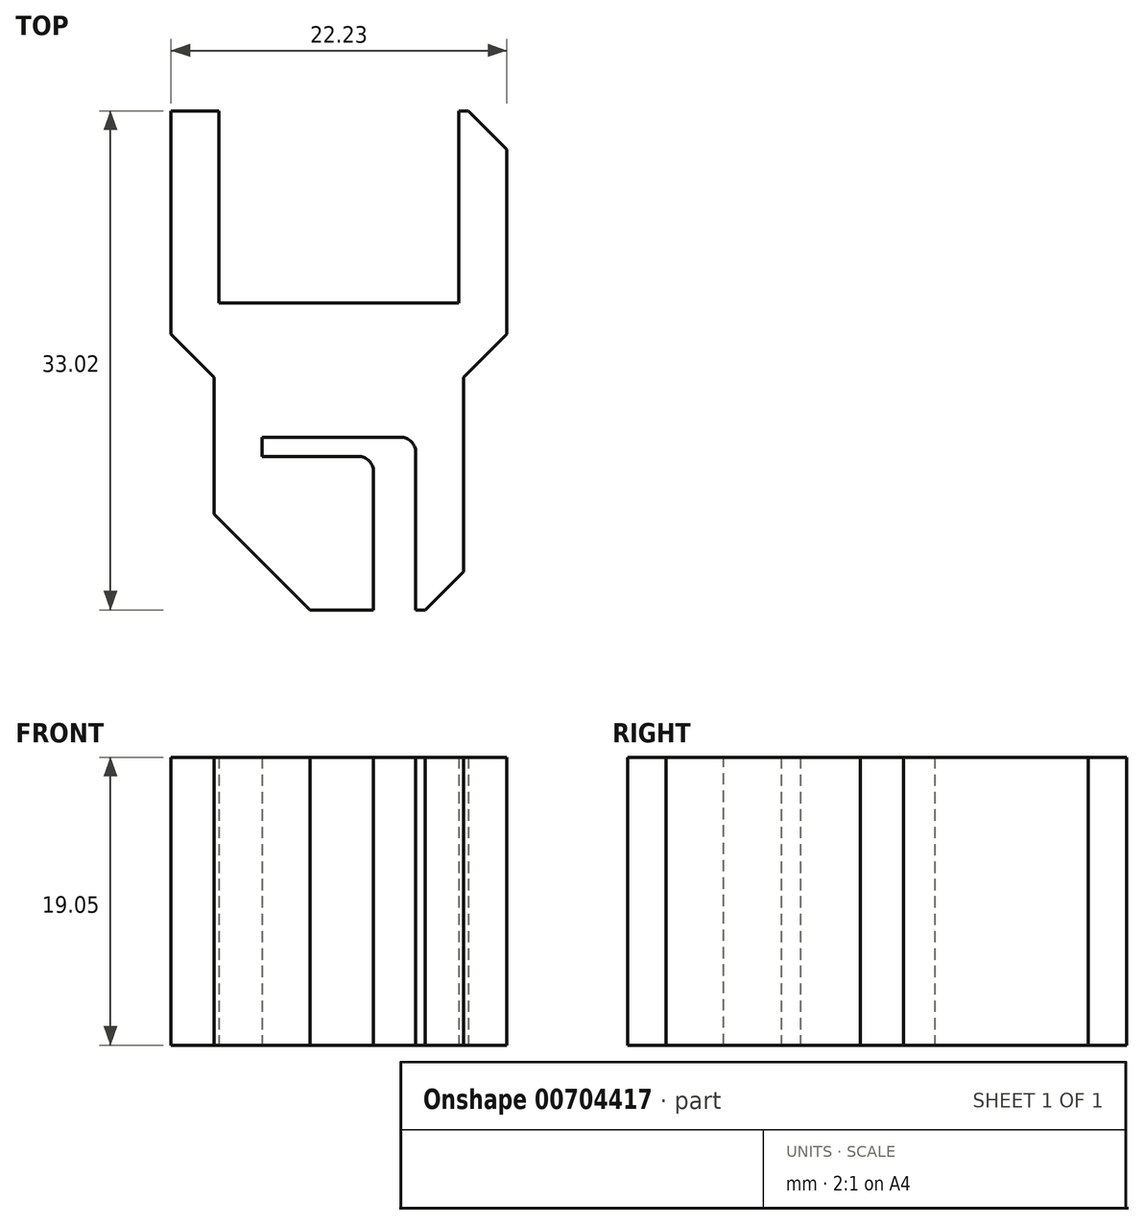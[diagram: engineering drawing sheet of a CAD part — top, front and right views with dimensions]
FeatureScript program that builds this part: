
annotation { "Feature Type Name" : "Feature", "Feature Type Description" : "" }
export const myFeature = defineFeature(function(context is Context, id is Id, definition is map)
    precondition{}
    {
        {
            var Q0;
            Q0=qCreatedBy(makeId("Top.planeOp"),FACE);
            var sketch = newSketch(context, id + "F0", { "sketchPlane" : qUnion([Q0])});
            skLineSegment(sketch, "E0", {"start": v(0, 0) * mm, "end": v(0, 20.47) * mm});
            skLineSegment(sketch, "E1", {"start": v(0, 20.47) * mm, "end": v(-2.86, 20.47) * mm});
            skLineSegment(sketch, "E2", {"start": v(-2.86, 20.47) * mm, "end": v(-2.86, 33.02) * mm});
            skLineSegment(sketch, "E3", {"start": v(-2.86, 33.02) * mm, "end": v(0.32, 33.02) * mm});
            skLineSegment(sketch, "E4", {"start": v(0.32, 33.02) * mm, "end": v(0.32, 20.32) * mm});
            skLineSegment(sketch, "E5", {"start": v(0.32, 20.32) * mm, "end": v(8.26, 20.32) * mm});
            skLineSegment(sketch, "E6", {"start": v(0, 0) * mm, "end": v(3.18, 0) * mm});
            skLineSegment(sketch, "E7", {"start": v(3.18, 0) * mm, "end": v(3.18, 11.43) * mm});
            skLineSegment(sketch, "E8", {"start": v(3.18, 11.43) * mm, "end": v(8.26, 11.43) * mm});
            skLineSegment(sketch, "E9", {"start": v(8.26, 20.32) * mm, "end": v(8.26, 11.43) * mm, "construction": true});
            skLineSegment(sketch, "E10.MirrorCS", {"start": v(13.34, 11.43) * mm, "end": v(8.26, 11.43) * mm});
            skLineSegment(sketch, "E11.MirrorCS", {"start": v(16.51, 20.47) * mm, "end": v(19.37, 20.47) * mm});
            skLineSegment(sketch, "E12.MirrorCS", {"start": v(19.37, 33.02) * mm, "end": v(16.2, 33.02) * mm});
            skLineSegment(sketch, "E13.MirrorCS", {"start": v(16.51, 0) * mm, "end": v(13.34, 0) * mm});
            skLineSegment(sketch, "E14.MirrorCS", {"start": v(19.37, 20.47) * mm, "end": v(19.37, 33.02) * mm});
            skLineSegment(sketch, "E15.MirrorCS", {"start": v(16.2, 20.32) * mm, "end": v(8.26, 20.32) * mm});
            skLineSegment(sketch, "E16.MirrorCS", {"start": v(16.2, 33.02) * mm, "end": v(16.2, 20.32) * mm});
            skLineSegment(sketch, "E17.MirrorCS", {"start": v(13.33, 0) * mm, "end": v(13.34, 11.43) * mm});
            skLineSegment(sketch, "E18.MirrorCS", {"start": v(16.51, 0) * mm, "end": v(16.51, 20.47) * mm});
            skLineSegment(sketch, "E19", {"start": v(10.54, 10.16) * mm, "end": v(3.18, 10.16) * mm});
            skLineSegment(sketch, "E20", {"start": v(10.54, 10.16) * mm, "end": v(10.54, 0) * mm});
            skLineSegment(sketch, "E21", {"start": v(3.18, 0) * mm, "end": v(10.54, 0) * mm});
            skSolve(sketch);
        }
        {
            var Q0;
            Q0 = qSketchRegion(id + "F0", true);
            extrude(context, id + "F1", {"entities" : qUnion([Q0]), "depth" : 19.05 * mm, "offsetDistance" : 25.4 * mm});
        }
        {
            var Q0;
            Q0=makeQuery(id+"F1.opExtrude","SWEPT_EDGE",EDGE,{"disambiguationData":[OSD([sQuery(id+"F0.wireOp",EDGE,"E0"),sQuery(id+"F0.wireOp",EDGE,"E1")])]});
            var Q1;
            Q1=makeQuery(id+"F1.opExtrude","SWEPT_EDGE",EDGE,{"disambiguationData":[OSD([sQuery(id+"F0.wireOp",EDGE,"E11.MirrorCS"),sQuery(id+"F0.wireOp",EDGE,"E18.MirrorCS")])]});
            chamfer(context, id + "F2", {"entities" : qUnion([Q0, Q1]), "width" : 5.08 * mm, "tangentPropagation" : true});
        }
        {
            var Q0;
            Q0=makeQuery(id+"F1.opExtrude","SWEPT_EDGE",EDGE,{"disambiguationData":[OSD([sQuery(id+"F0.wireOp",EDGE,"E13.MirrorCS"),sQuery(id+"F0.wireOp",EDGE,"E18.MirrorCS")])]});
            var Q1;
            Q1=makeQuery(id+"F1.opExtrude","SWEPT_EDGE",EDGE,{"disambiguationData":[OSD([sQuery(id+"F0.wireOp",EDGE,"E12.MirrorCS"),sQuery(id+"F0.wireOp",EDGE,"E14.MirrorCS")])]});
            chamfer(context, id + "F3", {"entities" : qUnion([Q0, Q1]), "width" : 2.54 * mm, "tangentPropagation" : true});
        }
        {
            var Q0;
            Q0=makeQuery(id+"F1.opExtrude","SWEPT_EDGE",EDGE,{"disambiguationData":[OSD([sQuery(id+"F0.wireOp",EDGE,"E0"),sQuery(id+"F0.wireOp",EDGE,"E6")])]});
            chamfer(context, id + "F4", {"entities" : qUnion([Q0]), "width" : 6.35 * mm, "tangentPropagation" : true});
        }
        {
            var Q0;
            Q0=makeQuery(id+"F1.opExtrude","SWEPT_EDGE",EDGE,{"disambiguationData":[OSD([sQuery(id+"F0.wireOp",EDGE,"E10.MirrorCS"),sQuery(id+"F0.wireOp",EDGE,"E17.MirrorCS")])]});
            var Q1;
            Q1=makeQuery(id+"F1.opExtrude","SWEPT_EDGE",EDGE,{"disambiguationData":[OSD([sQuery(id+"F0.wireOp",EDGE,"E19"),sQuery(id+"F0.wireOp",EDGE,"E20")])]});
            fillet(context, id + "F5", {"entities" : qUnion([Q0, Q1]), "tangentPropagation" : true, "radius" : 1.02 * mm, "defaultsChanged" : true, "vertexSettings" : [], "allowEdgeOverflow" : false});
        }
    });
